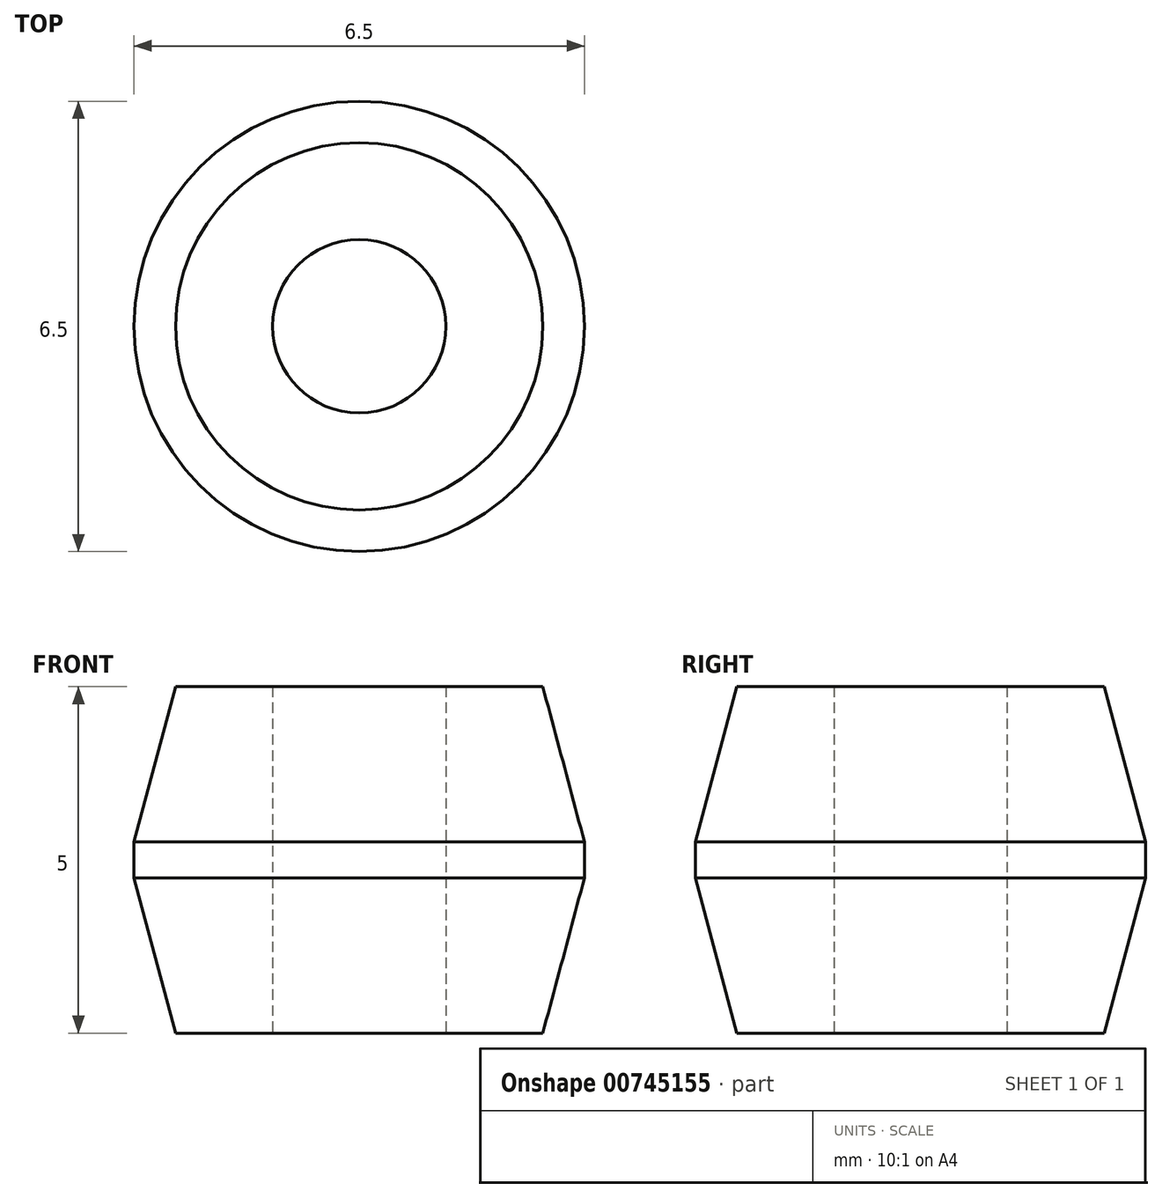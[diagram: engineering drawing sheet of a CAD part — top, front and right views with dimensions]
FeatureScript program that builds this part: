
annotation { "Feature Type Name" : "Feature", "Feature Type Description" : "" }
export const myFeature = defineFeature(function(context is Context, id is Id, definition is map)
    precondition{}
    {
        {
            var Q0;
            Q0=qCreatedBy(makeId("Top.planeOp"),FACE);
            var sketch = newSketch(context, id + "F0", { "sketchPlane" : qUnion([Q0])});
            skCircle(sketch, "E0", {"center": v(0, 0) * mm, "radius": 1.25 * mm});
            skCircle(sketch, "E1", {"center": v(0, 0) * mm, "radius": 3.25 * mm});
            skCircle(sketch, "E2", {"center": v(0, 0) * mm, "radius": 2.9 * mm});
            skSolve(sketch);
        }
        {
            var Q0;
            Q0=makeQuery(id+"F0.imprint","IMPRINT",FACE,{"disambiguationData":[TD([[makeQuery(id+"F0.imprint","IMPRINT",EDGE,{"derivedFrom":sQuery(id+"F0.wireOp",EDGE,"E0")}),-1.0]])]});
            var Q1;
            Q1=makeQuery(id+"F0.imprint","IMPRINT",FACE,{"disambiguationData":[TD([[makeQuery(id+"F0.imprint","IMPRINT",EDGE,{"derivedFrom":sQuery(id+"F0.wireOp",EDGE,"E1")}),1.0]])]});
            extrude(context, id + "F1", {"entities" : qUnion([Q0, Q1]), "depth" : 5 * mm, "offsetDistance" : 25 * mm});
        }
        {
            var Q0;
            Q0=makeQuery(id+"F1.opExtrude","CAP_EDGE",EDGE,{"disambiguationData":[OSD([sQuery(id+"F0.wireOp",EDGE,"E2")])],"isStart":false});
            var Q1;
            Q1=makeQuery(id+"F1.opExtrude","CAP_EDGE",EDGE,{"disambiguationData":[OSD([sQuery(id+"F0.wireOp",EDGE,"E2")])],"isStart":true});
            var Q2;
            Q2=makeQuery(id+"F1.opExtrude","CAP_EDGE",EDGE,{"disambiguationData":[OSD([sQuery(id+"F0.wireOp",EDGE,"E1")])],"isStart":false});
            var Q3;
            Q3=makeQuery(id+"F1.opExtrude","CAP_EDGE",EDGE,{"disambiguationData":[OSD([sQuery(id+"F0.wireOp",EDGE,"E1")])],"isStart":true});
            chamfer(context, id + "F2", {"entities" : qUnion([Q0, Q1, Q2, Q3]), "chamferType" : ChamferType.OFFSET_ANGLE, "width" : .6 * mm, "oppositeDirection" : false, "angle" : 75 * degree});
        }
    });
